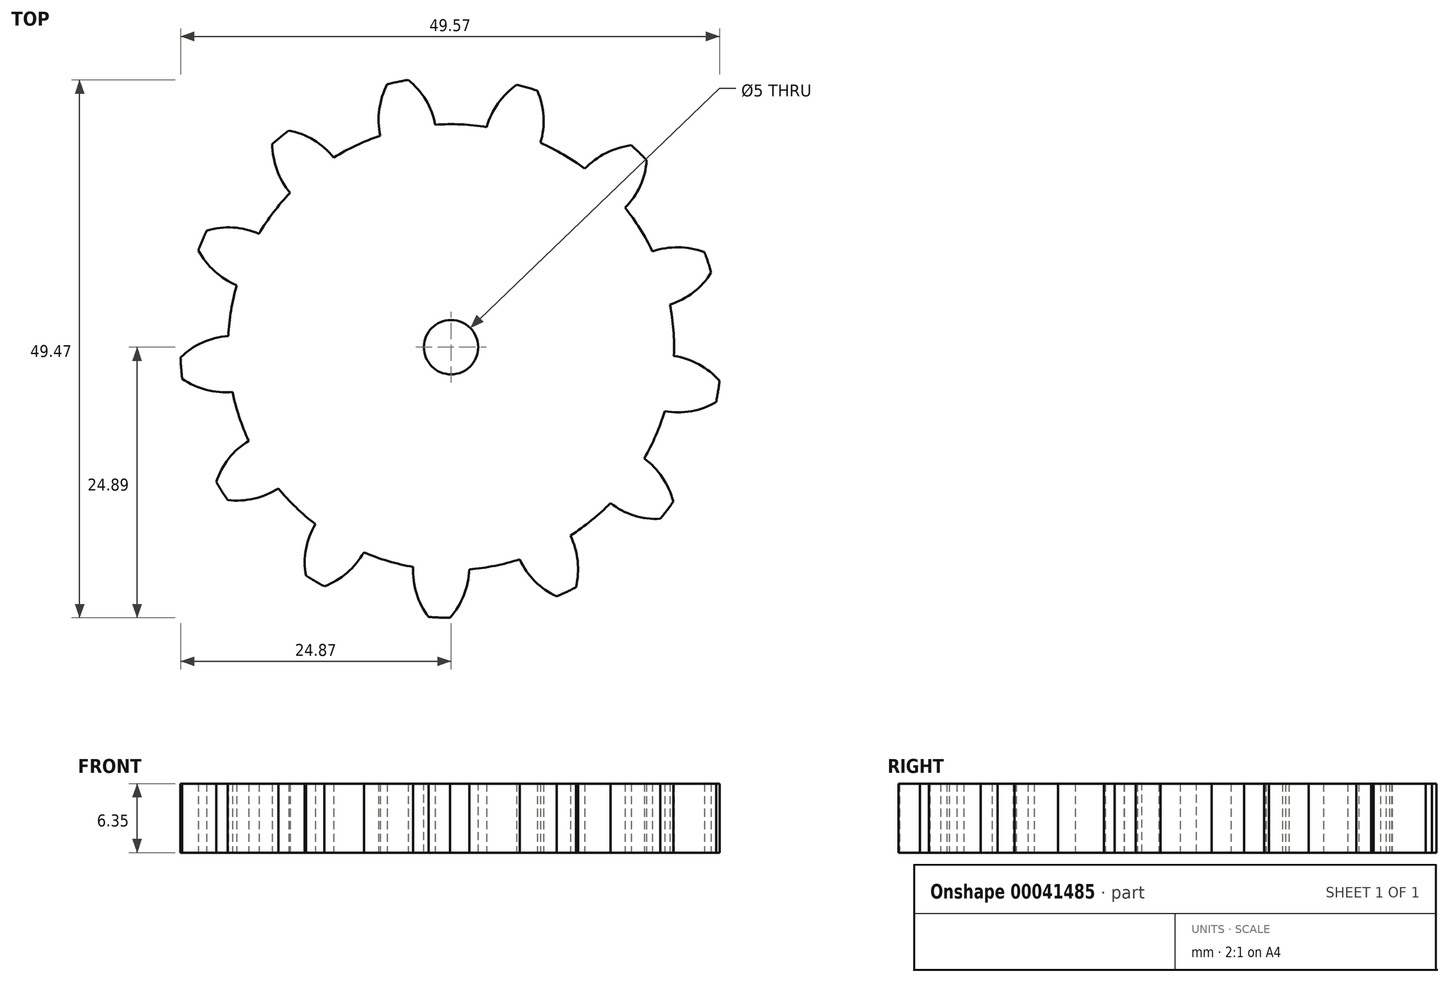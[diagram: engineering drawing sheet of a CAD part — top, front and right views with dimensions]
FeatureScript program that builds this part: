
annotation { "Feature Type Name" : "Feature", "Feature Type Description" : "" }
export const myFeature = defineFeature(function(context is Context, id is Id, definition is map)
    precondition{}
    {
        {
            var Q0;
            Q0=qCreatedBy(makeId("Top.planeOp"),FACE);
            var sketch = newSketch(context, id + "F0", { "sketchPlane" : qUnion([Q0])});
            skCircle(sketch, "E0", {"center": v(0, 0) * mm, "radius": 25.4 * mm, "construction": true});
            skCircle(sketch, "E1", {"center": v(0, 0) * mm, "radius": 24.9 * mm});
            skCircle(sketch, "E2", {"center": v(0, 0) * mm, "radius": 22.13 * mm, "construction": true});
            skCircle(sketch, "E3", {"center": v(0, 0) * mm, "radius": 20.9 * mm, "construction": true});
            skLineSegment(sketch, "E4", {"start": v(0, 20.9) * mm, "end": v(0, 25.4) * mm, "construction": true});
            skLineSegment(sketch, "E5", {"start": v(-6.36, 24.6) * mm, "end": v(-5.23, 20.23) * mm, "construction": true});
            skLineSegment(sketch, "E6", {"start": v(-5.23, 20.23) * mm, "end": v(0, 22.13) * mm, "construction": true});
            skLineSegment(sketch, "E7", {"start": v(-13.83, 20.7) * mm, "end": v(-14.11, 21.12) * mm});
            skLineSegment(sketch, "E8", {"start": v(0, 22.13) * mm, "end": v(6.63, 24.52) * mm, "construction": true});
            skLineSegment(sketch, "E9", {"start": v(10.24, 18.22) * mm, "end": v(3.9, 21.78) * mm, "construction": true});
            skCircle(sketch, "E10", {"center": v(10.24, 18.22) * mm, "radius": 7.26 * mm});
            skLineSegment(sketch, "E11", {"start": v(3.9, 21.78) * mm, "end": v(4.4, 24.5) * mm, "construction": true});
            skLineSegment(sketch, "E12", {"start": v(15.28, 19.65) * mm, "end": v(13.58, 17.47) * mm, "construction": true});
            skLineSegment(sketch, "E13", {"start": v(10.13, 22.74) * mm, "end": v(9, 20.21) * mm, "construction": true});
            skLineSegment(sketch, "E14", {"start": v(3.9, 21.78) * mm, "end": v(10.13, 22.74) * mm, "construction": true});
            skLineSegment(sketch, "E15", {"start": v(13.58, 17.47) * mm, "end": v(10.13, 22.74) * mm, "construction": true});
            skCircle(sketch, "E16", {"center": v(0, 0) * mm, "radius": 20.5 * mm});
            skLineSegment(sketch, "E17", {"start": v(5.68, 19.55) * mm, "end": v(3.26, 20.25) * mm, "construction": true});
            skLineSegment(sketch, "E18", {"start": v(9, 20.21) * mm, "end": v(8.5, 20.25) * mm});
            skLineSegment(sketch, "E19", {"start": v(8.5, 20.25) * mm, "end": v(1.77, 20.83) * mm, "construction": true});
            skCircle(sketch, "E20", {"center": v(1.77, 20.83) * mm, "radius": 6.75 * mm});
            skLineSegment(sketch, "E21", {"start": v(5.68, 19.55) * mm, "end": v(7.21, 24.82) * mm, "construction": true});
            skLineSegment(sketch, "E22", {"start": v(9, 20.21) * mm, "end": v(3.9, 21.78) * mm, "construction": true});
            skSolve(sketch);
        }
        {
            var Q0;
            {var subQ0=sQuery(id+"F0.wireOp",EDGE,"E20");var subQ3=sQuery(id+"F0.wireOp",EDGE,"E10");var subQ4=makeQuery(id+"F0.imprint","INTERSECT",VERTEX,{"disambiguationData":[OD(1.0)],"derivedFrom":[subQ3,subQ0]});Q0=makeQuery(id+"F0.imprint","IMPRINT",FACE,{"disambiguationData":[TD([[makeQuery(id+"F0.imprint","IMPRINT",EDGE,{"disambiguationData":[TD([[subQ4,-1.0]])],"derivedFrom":subQ3}),-1.0]])]});}
            var Q1;
            {var subQ0=sQuery(id+"F0.wireOp",EDGE,"E20");var subQ3=sQuery(id+"F0.wireOp",EDGE,"E10");var subQ4=makeQuery(id+"F0.imprint","INTERSECT",VERTEX,{"disambiguationData":[OD(1.0)],"derivedFrom":[subQ3,subQ0]});Q1=makeQuery(id+"F0.imprint","IMPRINT",FACE,{"disambiguationData":[TD([[makeQuery(id+"F0.imprint","IMPRINT",EDGE,{"disambiguationData":[TD([[subQ4,-1.0]])],"derivedFrom":subQ3}),1.0]])]});}
            var Q2;
            {var subQ1=sQuery(id+"F0.wireOp",EDGE,"E16");var subQ3=sQuery(id+"F0.wireOp",EDGE,"E10");var subQ5=makeQuery(id+"F0.imprint","INTERSECT",VERTEX,{"disambiguationData":[OD(0.0)],"derivedFrom":[subQ3,subQ1]});Q2=makeQuery(id+"F0.imprint","IMPRINT",FACE,{"disambiguationData":[TD([[makeQuery(id+"F0.imprint","IMPRINT",EDGE,{"disambiguationData":[TD([[subQ5,-1.0]])],"derivedFrom":subQ3}),1.0]])]});}
            var Q3;
            {var subQ1=sQuery(id+"F0.wireOp",EDGE,"E16");var subQ3=sQuery(id+"F0.wireOp",EDGE,"E10");var subQ5=makeQuery(id+"F0.imprint","INTERSECT",VERTEX,{"disambiguationData":[OD(0.0)],"derivedFrom":[subQ3,subQ1]});Q3=makeQuery(id+"F0.imprint","IMPRINT",FACE,{"disambiguationData":[TD([[makeQuery(id+"F0.imprint","IMPRINT",EDGE,{"disambiguationData":[TD([[subQ5,-1.0]])],"derivedFrom":subQ3}),-1.0]])]});}
            var Q4;
            {var subQ0=sQuery(id+"F0.wireOp",EDGE,"E20");var subQ3=makeQuery(id+"F0.imprint","IMPRINT",VERTEX,{"derivedFrom":subQ0});Q4=makeQuery(id+"F0.imprint","IMPRINT",FACE,{"disambiguationData":[TD([[makeQuery(id+"F0.imprint","IMPRINT",EDGE,{"disambiguationData":[TD([[subQ3,-1.0]])],"derivedFrom":subQ0}),1.0]])]});}
            extrude(context, id + "F1", {"entities" : qUnion([Q0, Q1, Q2, Q3, Q4]), "depth" : 6.35 * mm});
        }
        {
            var Q0;
            Q0=makeQuery(id+"F1.opExtrude","SWEPT_BODY",BODY,{"disambiguationData":[OSD([sQuery(id+"F0.wireOp",EDGE,"E1"),sQuery(id+"F0.wireOp",EDGE,"E10"),sQuery(id+"F0.wireOp",EDGE,"E16"),sQuery(id+"F0.wireOp",EDGE,"E20")])]});
            var Q1;
            Q1=makeQuery(id+"F1.opExtrude","CAP_EDGE",EDGE,{"disambiguationData":[OSD([sQuery(id+"F0.wireOp",EDGE,"E16")])],"isStart":false});
            circularPattern(context, id + "F2", {"operationType" : NewBodyOperationType.ADD, "entities" : qUnion([Q0]), "axis" : qUnion([Q1]), "angle" : 360 * degree, "instanceCount" : round(13), "equalSpace" : true});
        }
        {
            var Q0;
            {var subQ0=makeQuery(id+"F1.opExtrude","CAP_FACE",FACE,{"disambiguationData":[OSD([sQuery(id+"F0.wireOp",EDGE,"E1"),sQuery(id+"F0.wireOp",EDGE,"E10"),sQuery(id+"F0.wireOp",EDGE,"E16"),sQuery(id+"F0.wireOp",EDGE,"E20")])],"isStart":false});Q0=makeQuery(id+"F2.boolean.opBoolean","MERGE",FACE,{"derivedFrom":[subQ0,makeQuery(id+"F2.opPattern","COPY",FACE,{"derivedFrom":subQ0,"instanceName":"1"}),makeQuery(id+"F2.opPattern","COPY",FACE,{"derivedFrom":subQ0,"instanceName":"2"}),makeQuery(id+"F2.opPattern","COPY",FACE,{"derivedFrom":subQ0,"instanceName":"3"}),makeQuery(id+"F2.opPattern","COPY",FACE,{"derivedFrom":subQ0,"instanceName":"4"}),makeQuery(id+"F2.opPattern","COPY",FACE,{"derivedFrom":subQ0,"instanceName":"5"}),makeQuery(id+"F2.opPattern","COPY",FACE,{"derivedFrom":subQ0,"instanceName":"6"}),makeQuery(id+"F2.opPattern","COPY",FACE,{"derivedFrom":subQ0,"instanceName":"7"}),makeQuery(id+"F2.opPattern","COPY",FACE,{"derivedFrom":subQ0,"instanceName":"8"}),makeQuery(id+"F2.opPattern","COPY",FACE,{"derivedFrom":subQ0,"instanceName":"9"}),makeQuery(id+"F2.opPattern","COPY",FACE,{"derivedFrom":subQ0,"instanceName":"10"}),makeQuery(id+"F2.opPattern","COPY",FACE,{"derivedFrom":subQ0,"instanceName":"11"}),makeQuery(id+"F2.opPattern","COPY",FACE,{"derivedFrom":subQ0,"instanceName":"12"})]});}
            var sketch = newSketch(context, id + "F3", { "sketchPlane" : qUnion([Q0])});
            skCircle(sketch, "E23", {"center": v(0, 0) * mm, "radius": 2.5 * mm});
            skSolve(sketch);
        }
        {
            var Q0;
            Q0=makeQuery(id+"F3.imprint","IMPRINT",FACE,{"disambiguationData":[TD([[makeQuery(id+"F3.imprint","IMPRINT",EDGE,{"derivedFrom":sQuery(id+"F3.wireOp",EDGE,"E23")}),1.0]])]});
            extrude(context, id + "F4", {"entities" : qUnion([Q0]), "operationType" : NewBodyOperationType.REMOVE, "oppositeDirection" : true, "depth" : 25.4 * mm});
        }
    });
